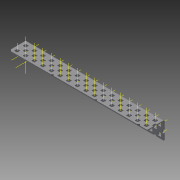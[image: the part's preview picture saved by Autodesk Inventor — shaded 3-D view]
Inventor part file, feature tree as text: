
AUTODESK INVENTOR PART (.ipt)
format: ipt  version: 2015 (Build 190159000, 159)  size: 2,095,104 bytes
history: native  units: in
note: dims shown in document units (in); Inventor stores cm internally (conversion verified against a paired STEP export)
features: other x101, pattern_linear x4, sheet_metal_op x1, extrude x1, imported_body x1, sketch x1
ambient origin geometry x8: Origin, YZ Plane, XZ Plane, XY Plane, X Axis, Y Axis, Z Axis, Center Point
bodies: Body1 (feature_tree)
feature tree (109):
  sheet_metal_op  "Fold1"
  other  "L-Channel"
  extrude  "length cut"  Depth=0.5in
  other  "top out axis"
  other  "top inner axis"
  other  "back out axis"
  other  "back inner axis"
  pattern_linear  "top outer axes"  Count1=2 Spacing1=0.5in
  pattern_linear  "top inner axes"  Spacing1=0.5in  [1 undecoded]
  pattern_linear  "back outer axes"  Count1=2 Spacing1=0.5in
  pattern_linear  "back inner axes"  Spacing1=0.5in  [1 undecoded]
  other  "right plane"
  imported_body  "Base1"
  sketch  "Sketch1"  dims[d1=0.0in d4=0.5in d5=0.7874in d7=0.5in d10=0.5in d13=0.5in d14=0.7874in d16=0.5in d19=0.5in d20=-8.0in d21=0.0in d22=0.0in d23=0.0in d24=0.0in d25=0.0in d26=0.0in]
  other  "Work Point1"
  other  "Work Point2"
  other  "Work Point3"
  other  "Work Point4"
  other  "Work Axis5"
  other  "Work Axis6"
  other  "Work Axis7"
  other  "Work Axis8"
  other  "Work Axis11"
  other  "Work Axis12"
  other  "Work Axis13"
  other  "Work Axis14"
  other  "Work Axis15"
  other  "Work Axis18"
  other  "Work Axis19"
  other  "Work Axis20"
  other  "Work Axis23"
  other  "Work Axis24"
  other  "Work Axis25"
  other  "Work Axis26"
  other  "Work Axis29"
  other  "Work Axis30"
  other  "Work Axis31"
  other  "Work Axis32"
  other  "Work Axis33"
  other  "Work Axis36"
  other  "Work Axis37"
  other  "Work Axis38"
  other  "Work Axis41"
  other  "Work Axis42"
  other  "Work Axis43"
  other  "Work Axis44"
  other  "Work Axis45"
  other  "Work Axis61"
  other  "Work Axis62"
  other  "Work Axis63"
  other  "Work Axis64"
  other  "Work Axis65"
  other  "Work Axis81"
  other  "Work Axis82"
  other  "Work Axis83"
  other  "Work Axis84"
  other  "Work Axis85"
  other  "Work Axis101"
  other  "Work Axis102"
  other  "Work Axis103"
  other  "Work Axis104"
  other  "Work Axis105"
  other  "Work Axis121"
  other  "Work Axis122"
  other  "Work Axis123"
  other  "Work Axis124"
  other  "Work Axis125"
  other  "Work Axis141"
  other  "Work Axis142"
  other  "Work Axis143"
  other  "Work Axis144"
  other  "Work Axis145"
  other  "left plane"
  other  "Work Axis161"
  other  "Work Axis162"
  other  "Work Axis163"
  other  "Work Axis164"
  other  "Work Axis165"
  other  "Work Axis166"
  other  "Work Axis167"
  other  "Work Axis168"
  other  "Work Axis169"
  other  "Work Axis170"
  other  "Work Axis171"
  other  "Work Axis172"
  other  "Work Axis173"
  other  "Work Axis174"
  other  "Work Axis175"
  other  "Work Axis176"
  other  "Work Axis177"
  other  "Work Axis178"
  other  "Work Axis179"
  other  "Work Axis180"
  other  "Work Axis181"
  other  "Work Axis182"
  other  "Work Axis183"
  other  "Work Axis184"
  other  "Work Axis185"
  other  "Work Axis186"
  other  "Work Axis187"
  other  "Work Axis188"
  other  "Work Axis189"
  other  "Work Axis190"
  other  "Work Axis191"
  other  "Work Axis192"
  other  "Work Axis193"
  other  "Work Axis194"
  other  "Work Axis195"
  other  "Work Axis196"
note: 2 required parameter values undecoded (feature->parameter linkage not recoverable at this tier; creation-order binding heuristic only, values carry confidence <= 0.55)
